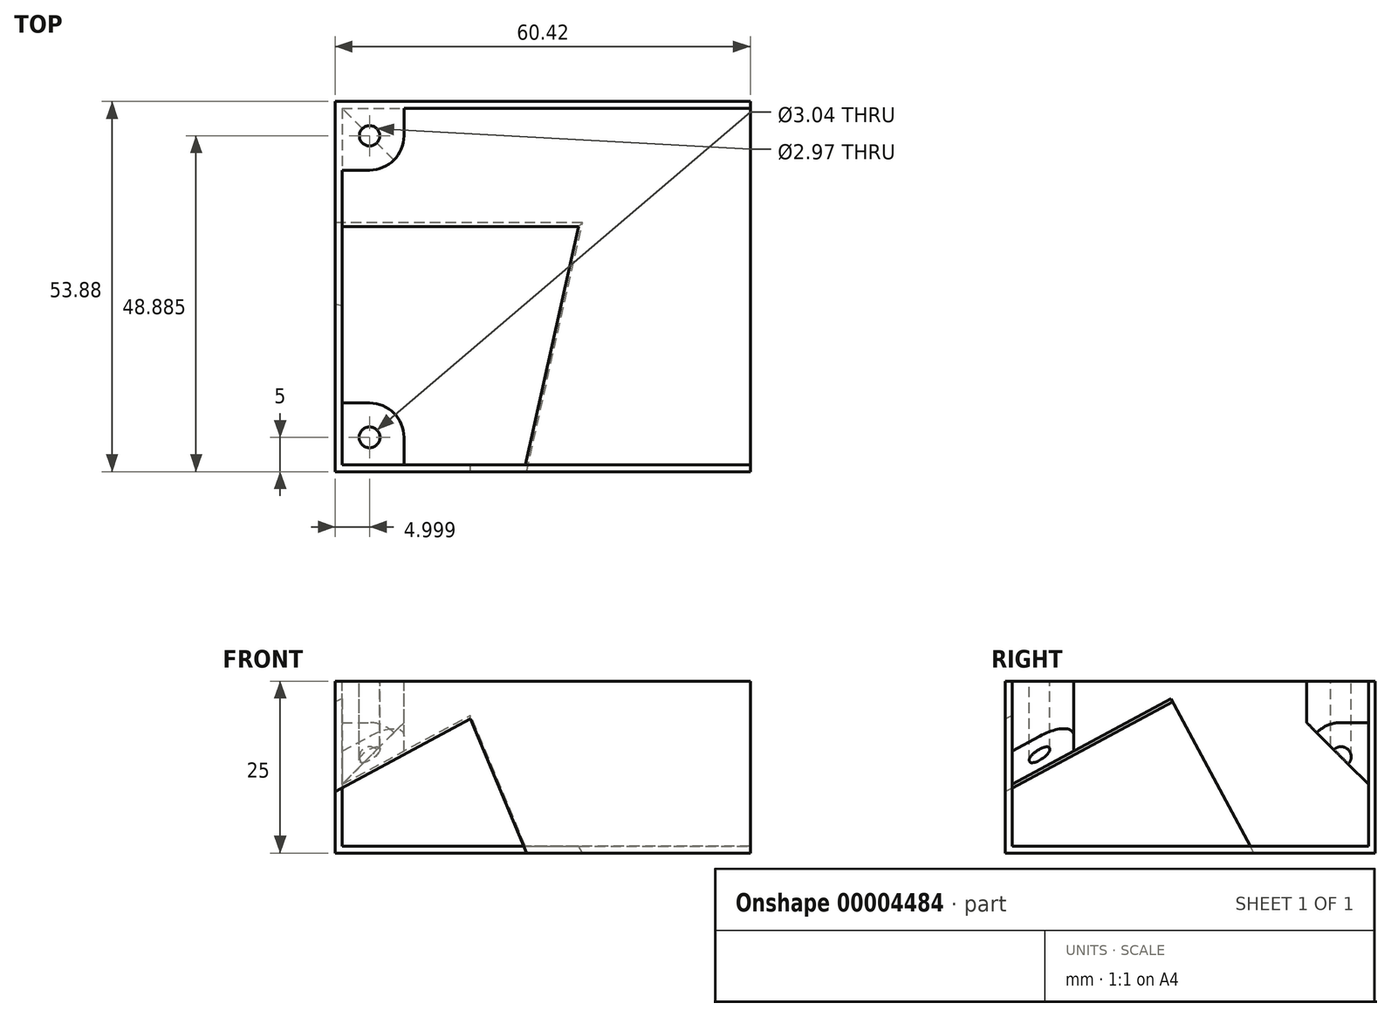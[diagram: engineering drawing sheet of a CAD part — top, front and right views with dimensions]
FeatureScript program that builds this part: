
annotation { "Feature Type Name" : "Feature", "Feature Type Description" : "" }
export const myFeature = defineFeature(function(context is Context, id is Id, definition is map)
    precondition{}
    {
        {
            var Q0;
            Q0=qCreatedBy(makeId("Top.planeOp"),FACE);
            var sketch = newSketch(context, id + "F0", { "sketchPlane" : qUnion([Q0])});
            skLineSegment(sketch, "E0.bottom", {"start": v(0, 0) * mm, "end": v(-60.42, 0) * mm});
            skLineSegment(sketch, "E0.top", {"start": v(0, 53.88) * mm, "end": v(-60.42, 53.88) * mm});
            skLineSegment(sketch, "E0.left", {"start": v(0, 0) * mm, "end": v(0, 53.88) * mm});
            skLineSegment(sketch, "E0.right", {"start": v(-60.42, 0) * mm, "end": v(-60.42, 53.88) * mm});
            skSolve(sketch);
        }
        {
            var Q0;
            Q0 = qSketchRegion(id + "F0", true);
            extrude(context, id + "F1", {"entities" : qUnion([Q0]), "depth" : 25 * mm});
        }
        {
            var Q0;
            Q0=makeQuery(id+"F1.opExtrude","CAP_FACE",FACE,{"disambiguationData":[OSD([sQuery(id+"F0.wireOp",EDGE,"E0.bottom"),sQuery(id+"F0.wireOp",EDGE,"E0.top"),sQuery(id+"F0.wireOp",EDGE,"E0.left"),sQuery(id+"F0.wireOp",EDGE,"E0.right")])],"isStart":false});
            var sketch = newSketch(context, id + "F2", { "sketchPlane" : qUnion([Q0])});
            skLineSegment(sketch, "E1.bottom", {"start": v(-59.42, 52.88) * mm, "end": v(0, 52.88) * mm});
            skLineSegment(sketch, "E1.top", {"start": v(-59.42, 0) * mm, "end": v(0, 0) * mm});
            skLineSegment(sketch, "E1.left", {"start": v(-59.42, 52.88) * mm, "end": v(-59.42, 0) * mm});
            skLineSegment(sketch, "E1.right", {"start": v(0, 52.88) * mm, "end": v(0, 0) * mm});
            skSolve(sketch);
        }
        {
            var Q0;
            Q0 = qSketchRegion(id + "F2", true);
            extrude(context, id + "F3", {"entities" : qUnion([Q0]), "operationType" : NewBodyOperationType.REMOVE, "oppositeDirection" : true, "depth" : 24 * mm});
        }
        {
            var Q0;
            Q0=makeQuery(id+"F1.opExtrude","CAP_FACE",FACE,{"disambiguationData":[OSD([sQuery(id+"F0.wireOp",EDGE,"E0.bottom"),sQuery(id+"F0.wireOp",EDGE,"E0.top"),sQuery(id+"F0.wireOp",EDGE,"E0.left"),sQuery(id+"F0.wireOp",EDGE,"E0.right")])],"isStart":false});
            var sketch = newSketch(context, id + "F4", { "sketchPlane" : qUnion([Q0])});
            skLineSegment(sketch, "E2.bottom", {"start": v(-59.42, 52.88) * mm, "end": v(-50.42, 52.88) * mm});
            skLineSegment(sketch, "E2.top", {"start": v(-59.42, 43.88) * mm, "end": v(-50.42, 43.88) * mm});
            skLineSegment(sketch, "E2.left", {"start": v(-59.42, 52.88) * mm, "end": v(-59.42, 43.88) * mm});
            skLineSegment(sketch, "E2.right", {"start": v(-50.42, 52.88) * mm, "end": v(-50.42, 43.88) * mm});
            skSolve(sketch);
        }
        {
            var Q0;
            Q0 = qSketchRegion(id + "F4", true);
            extrude(context, id + "F5", {"entities" : qUnion([Q0]), "operationType" : NewBodyOperationType.ADD, "oppositeDirection" : true, "depth" : 15 * mm});
        }
        {
            var Q0;
            Q0=makeQuery(id+"F5.opExtrude","CAP_EDGE",EDGE,{"disambiguationData":[OSD([sQuery(id+"F4.wireOp",EDGE,"E2.top")])],"isStart":false});
            var Q1;
            Q1=makeQuery(id+"F5.opExtrude","CAP_EDGE",EDGE,{"disambiguationData":[OSD([sQuery(id+"F4.wireOp",EDGE,"E2.right")])],"isStart":false});
            chamfer(context, id + "F6", {"entities" : qUnion([Q0, Q1]), "width" : 9 * mm, "tangentPropagation" : true});
        }
        {
            var Q0;
            Q0=makeQuery(id+"F5.opExtrude","SWEPT_EDGE",EDGE,{"disambiguationData":[OSD([sQuery(id+"F4.wireOp",EDGE,"E2.top"),sQuery(id+"F4.wireOp",EDGE,"E2.right")])]});
            fillet(context, id + "F7", {"entities" : qUnion([Q0]), "radius" : 5 * mm, "tangentPropagation" : true, "allowEdgeOverflow" : false});
        }
        {
            var Q0;
            Q0=makeQuery(id+"F5.boolean.opBoolean","MERGE",FACE,{"derivedFrom":[makeQuery(id+"F1.opExtrude","CAP_FACE",FACE,{"disambiguationData":[OSD([sQuery(id+"F0.wireOp",EDGE,"E0.bottom"),sQuery(id+"F0.wireOp",EDGE,"E0.top"),sQuery(id+"F0.wireOp",EDGE,"E0.left"),sQuery(id+"F0.wireOp",EDGE,"E0.right")])],"isStart":false}),makeQuery(id+"F5.opExtrude","CAP_FACE",FACE,{"disambiguationData":[OSD([sQuery(id+"F4.wireOp",EDGE,"E2.bottom"),sQuery(id+"F4.wireOp",EDGE,"E2.top"),sQuery(id+"F4.wireOp",EDGE,"E2.left"),sQuery(id+"F4.wireOp",EDGE,"E2.right")])],"isStart":true})]});
            var sketch = newSketch(context, id + "F8", { "sketchPlane" : qUnion([Q0])});
            skCircle(sketch, "E3", {"center": v(-55.42, 48.88) * mm, "radius": 1.48 * mm});
            skSolve(sketch);
        }
        {
            var Q0;
            Q0 = qSketchRegion(id + "F8", true);
            var Q1;
            Q1=makeQuery(id+"F3.boolean.opBoolean","COPY",FACE,{"derivedFrom":makeQuery(id+"F3.opExtrude","CAP_FACE",FACE,{"disambiguationData":[OSD([sQuery(id+"F2.wireOp",EDGE,"E1.bottom"),sQuery(id+"F2.wireOp",EDGE,"E1.top"),sQuery(id+"F2.wireOp",EDGE,"E1.left"),sQuery(id+"F2.wireOp",EDGE,"E1.right")])],"isStart":false})});
            extrude(context, id + "F9", {"entities" : qUnion([Q0]), "operationType" : NewBodyOperationType.REMOVE, "endBound" : BoundingType.UP_TO_SURFACE, "oppositeDirection" : true, "endBoundEntityFace" : qUnion([Q1]), "depth" : 25 * mm});
        }
        {
            var Q0;
            Q0=makeQuery(id+"F1.opExtrude","SWEPT_FACE",FACE,{"disambiguationData":[OSD([sQuery(id+"F0.wireOp",EDGE,"E0.bottom")])]});
            var sketch = newSketch(context, id + "F10", { "sketchPlane" : qUnion([Q0])});
            skLineSegment(sketch, "E4.bottom", {"start": v(-59.42, 25) * mm, "end": v(0, 25) * mm});
            skLineSegment(sketch, "E4.top", {"start": v(-59.42, 1) * mm, "end": v(0, 1) * mm});
            skLineSegment(sketch, "E4.left", {"start": v(-59.42, 25) * mm, "end": v(-59.42, 1) * mm});
            skLineSegment(sketch, "E4.right", {"start": v(0, 25) * mm, "end": v(0, 1) * mm});
            skSolve(sketch);
        }
        {
            var Q0;
            Q0 = qSketchRegion(id + "F10", true);
            extrude(context, id + "F11", {"entities" : qUnion([Q0]), "operationType" : NewBodyOperationType.ADD, "oppositeDirection" : true, "depth" : 1 * mm});
        }
        {
            var Q0;
            Q0=makeQuery(id+"F11.boolean.opBoolean","MERGE",FACE,{"derivedFrom":[makeQuery(id+"F5.boolean.opBoolean","MERGE",FACE,{"derivedFrom":[makeQuery(id+"F1.opExtrude","CAP_FACE",FACE,{"disambiguationData":[OSD([sQuery(id+"F0.wireOp",EDGE,"E0.bottom"),sQuery(id+"F0.wireOp",EDGE,"E0.top"),sQuery(id+"F0.wireOp",EDGE,"E0.left"),sQuery(id+"F0.wireOp",EDGE,"E0.right")])],"isStart":false}),makeQuery(id+"F5.opExtrude","CAP_FACE",FACE,{"disambiguationData":[OSD([sQuery(id+"F4.wireOp",EDGE,"E2.bottom"),sQuery(id+"F4.wireOp",EDGE,"E2.top"),sQuery(id+"F4.wireOp",EDGE,"E2.left"),sQuery(id+"F4.wireOp",EDGE,"E2.right")])],"isStart":true})]}),makeQuery(id+"F11.opExtrude","SWEPT_FACE",FACE,{"disambiguationData":[OSD([sQuery(id+"F10.wireOp",EDGE,"E4.bottom")])]})]});
            var sketch = newSketch(context, id + "F12", { "sketchPlane" : qUnion([Q0])});
            skLineSegment(sketch, "E5.bottom", {"start": v(-59.42, 1) * mm, "end": v(-50.42, 1) * mm});
            skLineSegment(sketch, "E5.top", {"start": v(-59.42, 10) * mm, "end": v(-50.42, 10) * mm});
            skLineSegment(sketch, "E5.left", {"start": v(-59.42, 1) * mm, "end": v(-59.42, 10) * mm});
            skLineSegment(sketch, "E5.right", {"start": v(-50.42, 1) * mm, "end": v(-50.42, 10) * mm});
            skSolve(sketch);
        }
        {
            var Q0;
            Q0 = qSketchRegion(id + "F12", true);
            extrude(context, id + "F13", {"entities" : qUnion([Q0]), "oppositeDirection" : true, "depth" : 15 * mm});
        }
        {
            var Q0;
            Q0=makeQuery(id+"F13.opExtrude","SWEPT_EDGE",EDGE,{"disambiguationData":[OSD([sQuery(id+"F12.wireOp",EDGE,"E5.top"),sQuery(id+"F12.wireOp",EDGE,"E5.right")])]});
            fillet(context, id + "F14", {"entities" : qUnion([Q0]), "radius" : 5 * mm, "tangentPropagation" : true, "allowEdgeOverflow" : false});
        }
        {
            var Q0;
            Q0=makeQuery(id+"F13.opExtrude","SWEPT_FACE",FACE,{"disambiguationData":[OSD([sQuery(id+"F12.wireOp",EDGE,"E5.right")])]});
            var sketch = newSketch(context, id + "F15", { "sketchPlane" : qUnion([Q0])});
            skPoint(sketch, "E6", {"position": v(5, 17) * mm});
            skSolve(sketch);
        }
        {
            var Q0;
            Q0=makeQuery(id+"F13.opExtrude","SWEPT_FACE",FACE,{"disambiguationData":[OSD([sQuery(id+"F12.wireOp",EDGE,"E5.top")])]});
            var sketch = newSketch(context, id + "F16", { "sketchPlane" : qUnion([Q0])});
            skPoint(sketch, "E7", {"position": v(55.42, 17) * mm});
            skSolve(sketch);
        }
        {
            var Q0;
            Q0=makeQuery(id+"F13.opExtrude","CAP_VERTEX",VERTEX,{"disambiguationData":[OSD([sQuery(id+"F12.wireOp",EDGE,"E5.bottom"),sQuery(id+"F12.wireOp",EDGE,"E5.left")])],"isStart":false});
            var Q1;
            Q1=sQuery(id+"F15.wireOp",VERTEX,"E6");
            var Q2;
            Q2=sQuery(id+"F16.wireOp",VERTEX,"E7");
            cPlane(context, id + "F17", {"entities" : qUnion([Q0, Q1, Q2]), "cplaneType" : CPlaneType.THREE_POINT, "offset" : 150 * mm, "width" : 150 * mm, "height" : 150 * mm});
        }
        {
            var Q0;
            Q0=qCreatedBy(id+"F17.planeOp",FACE);
            var sketch = newSketch(context, id + "F18", { "sketchPlane" : qUnion([Q0])});
            skLineSegment(sketch, "E8.bottom", {"start": v(-29.43, 8.05) * mm, "end": v(-66.62, 8.05) * mm});
            skLineSegment(sketch, "E8.top", {"start": v(-29.43, -31.9) * mm, "end": v(-66.62, -31.9) * mm});
            skLineSegment(sketch, "E8.left", {"start": v(-29.43, 8.05) * mm, "end": v(-29.43, -31.9) * mm});
            skLineSegment(sketch, "E8.right", {"start": v(-66.62, 8.05) * mm, "end": v(-66.62, -31.9) * mm});
            skSolve(sketch);
        }
        {
            var Q0;
            Q0 = qSketchRegion(id + "F18", true);
            extrude(context, id + "F19", {"entities" : qUnion([Q0]), "operationType" : NewBodyOperationType.REMOVE, "endBound" : BoundingType.THROUGH_ALL, "depth" : 25 * mm});
        }
        {
            var Q0;
            Q0=makeQuery(id+"F13.opExtrude","CAP_FACE",FACE,{"disambiguationData":[OSD([sQuery(id+"F12.wireOp",EDGE,"E5.bottom"),sQuery(id+"F12.wireOp",EDGE,"E5.top"),sQuery(id+"F12.wireOp",EDGE,"E5.left"),sQuery(id+"F12.wireOp",EDGE,"E5.right")])],"isStart":true});
            var sketch = newSketch(context, id + "F20", { "sketchPlane" : qUnion([Q0])});
            skCircle(sketch, "E9", {"center": v(-55.42, 5) * mm, "radius": 1.52 * mm});
            skSolve(sketch);
        }
        {
            var Q0;
            Q0 = qSketchRegion(id + "F20", true);
            var Q1;
            Q1=makeQuery(id+"F3.boolean.opBoolean","COPY",FACE,{"derivedFrom":makeQuery(id+"F3.opExtrude","CAP_FACE",FACE,{"disambiguationData":[OSD([sQuery(id+"F2.wireOp",EDGE,"E1.bottom"),sQuery(id+"F2.wireOp",EDGE,"E1.top"),sQuery(id+"F2.wireOp",EDGE,"E1.left"),sQuery(id+"F2.wireOp",EDGE,"E1.right")])],"isStart":false})});
            extrude(context, id + "F21", {"entities" : qUnion([Q0]), "operationType" : NewBodyOperationType.REMOVE, "endBound" : BoundingType.UP_TO_SURFACE, "oppositeDirection" : true, "endBoundEntityFace" : qUnion([Q1]), "depth" : 25 * mm});
        }
    });
